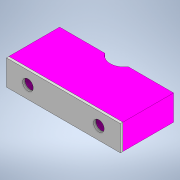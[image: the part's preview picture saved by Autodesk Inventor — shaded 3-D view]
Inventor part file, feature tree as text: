
AUTODESK INVENTOR PART (.ipt)
format: ipt  version: 2020 (Build 240168000, 168)  size: 135,680 bytes
history: native  units: mm
features: extrude x3, sketch x3
ambient origin geometry x8: Origin, YZ Plane, XZ Plane, XY Plane, X Axis, Y Axis, Z Axis, Center Point
bodies: Solid1 (feature_tree), Solid2 (feature_tree)
feature tree (6):
  extrude  "Extrusion1"  Depth=20.0mm
  extrude  "Extrusion2"  Depth=3.0mm
  extrude  "Extrusion3"  Depth=1.0mm
  sketch  "Sketch1"  dims[d0=45.0mm d1=20.0mm]
  sketch  "Sketch2"  dims[d2=5.5mm d3=3.0mm]
  sketch  "Sketch3"  dims[d4=10.0mm d5=0.0mm d6=4.2mm d7=8.5mm d8=5.0mm d9=0.0mm d10=0.0mm d11=1.0mm d12=0.0mm]
